# Revit family: Slim cassettes
name_source: partatom
category: Installations électriques
units: mm (PartAtom-declared; Revit-internal decimal feet)

## family parameters
Basée sur le plan de construction = Non
Conserver l'orientation des annotations = Non
Cote de connecteur circulaire = Utiliser le diamètre
Couper avec des vides une fois chargée = Non
Partagée = Non
Point de calcul de pièce = Non
Toujours verticalement = Oui
Type d'élément = Normal

## types (3) — shared parameters
Color = IDS_NOIR
Crossed = Oui
Depth = 194 mm  [stored 0.636483 ft]
E-catalogue link = https://www.legrand.fr
ETIM class = EC002699
Function = High density MTP cassettes
Height = 13.6 mm  [stored 0.0446194 ft]
Number of connectors front side = 12
Number of connectors rear side = 1
Operating temperature = -10°C à 60°C
Storage temperature = -10°C à 60°C
Type of connector external = LC_DUPLEX
Type of connector interior = MTP-M
Width (mm) = 100 mm  [stored 0.328084 ft]
zero-valued in all types: Elévation par défaut

## per-type parameters (varying)
| type | EAN | Fiber optic class | LC connectors | Legrand part number |
| Slim cassette 12 LC MTP OM3 HD panel Ultra | 3414971929333 | OM3 | Slim LC connectors : 12 fibers OM3 multimode | 032168 |
| Slim cassette 12 LC MTP OM4 HD panel Ultra | 3414971929135 | OM4 | Slim LC connectors : 12 fibers OM4 multi mode | 032169 |
| Slim cassette 12 LC MTP OS2 HD panel Ultra | 3414971929159 | OS2 | Slim LC connectors : 12 fibers OS2 single mode | 032170 |

note: column(s) folded — value = type name in every type: BIM wording

note: [stored X ft] marks values corroborated as IEEE doubles in the binary element streams (Revit-internal decimal feet)
